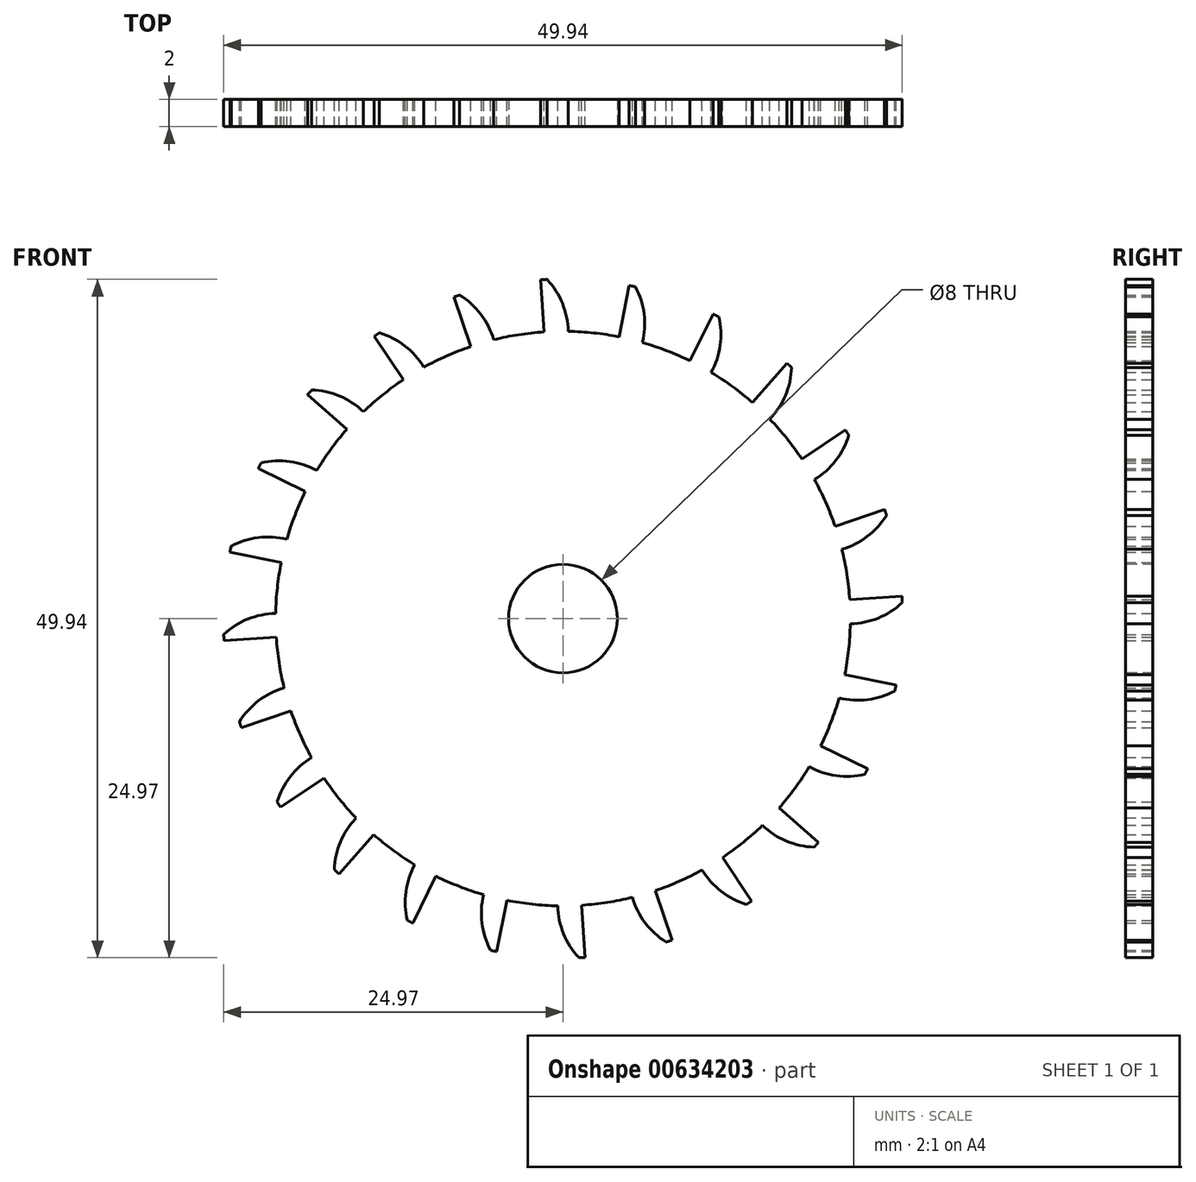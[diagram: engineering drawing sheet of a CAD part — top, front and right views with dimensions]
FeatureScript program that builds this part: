
annotation { "Feature Type Name" : "Feature", "Feature Type Description" : "" }
export const myFeature = defineFeature(function(context is Context, id is Id, definition is map)
    precondition{}
    {
        {
            var Q0;
            Q0=qCreatedBy(makeId("Front.planeOp"),FACE);
            var sketch = newSketch(context, id + "F0", { "sketchPlane" : qUnion([Q0])});
            skCircle(sketch, "E0", {"center": v(0, 0) * mm, "radius": 25 * mm, "construction": true});
            skCircle(sketch, "E1", {"center": v(0, 0) * mm, "radius": 23.1 * mm, "construction": true});
            skCircle(sketch, "E2", {"center": v(0, 0) * mm, "radius": 21.15 * mm});
            skLineSegment(sketch, "E3", {"start": v(0, 0) * mm, "end": v(0, 32.17) * mm, "construction": true});
            skLineSegment(sketch, "E4", {"start": v(0, 0) * mm, "end": v(-2.05, 31.22) * mm});
            skLineSegment(sketch, "E5", {"start": v(0, 23.1) * mm, "end": v(-31.77, 23.1) * mm, "construction": true});
            skLineSegment(sketch, "E6", {"start": v(0, 23.1) * mm, "end": v(-30.03, 12.17) * mm, "construction": true});
            skCircle(sketch, "E7", {"center": v(0, 0) * mm, "radius": 21.7 * mm, "construction": true});
            skCircle(sketch, "E8", {"center": v(0, 23.1) * mm, "radius": 5.75 * mm, "construction": true});
            skCircle(sketch, "E9", {"center": v(-5.37, 21.03) * mm, "radius": 5.75 * mm, "construction": true});
            skArc(sketch, "E10", {"start": v(0.38, 21.15) * mm, "mid": v(-0.04, 23.2) * mm, "end": v(-1.18, 24.97) * mm});
            skArc(sketch, "E11.MirrorCS", {"start": v(-3.14, 20.92) * mm, "mid": v(-2.99, 23.01) * mm, "end": v(-2.1, 24.91) * mm});
            skArc(sketch, "E12", {"start": v(-1.18, 24.97) * mm, "mid": v(-1.64, 24.95) * mm, "end": v(-2.1, 24.91) * mm});
            skSolve(sketch);
        }
        {
            var Q0;
            {var subQ0=sQuery(id+"F0.wireOp",EDGE,"E2");var subQ1=makeQuery(id+"F0.imprint","INTERSECT",VERTEX,{"derivedFrom":[subQ0,sQuery(id+"F0.wireOp",EDGE,"E10")]});Q0=makeQuery(id+"F0.imprint","IMPRINT",FACE,{"disambiguationData":[TD([[makeQuery(id+"F0.imprint","IMPRINT",EDGE,{"disambiguationData":[TD([[subQ1,-1.0]])],"derivedFrom":subQ0}),1.0]])]});}
            var Q1;
            {var subQ0=sQuery(id+"F0.wireOp",EDGE,"E11.MirrorCS");Q1=makeQuery(id+"F0.imprint","IMPRINT",FACE,{"disambiguationData":[TD([[makeQuery(id+"F0.imprint","IMPRINT",EDGE,{"derivedFrom":subQ0}),-1.0]])]});}
            var Q2;
            {var subQ0=sQuery(id+"F0.wireOp",EDGE,"E10");Q2=makeQuery(id+"F0.imprint","IMPRINT",FACE,{"disambiguationData":[TD([[makeQuery(id+"F0.imprint","IMPRINT",EDGE,{"derivedFrom":subQ0}),1.0]])]});}
            extrude(context, id + "F1", {"entities" : qUnion([Q0, Q1, Q2]), "depth" : 2 * mm, "offsetDistance" : 25 * mm});
        }
        {
            var Q0;
            Q0=makeQuery(id+"F1.opExtrude","SWEPT_BODY",BODY,{"disambiguationData":[OSD([sQuery(id+"F0.wireOp",EDGE,"E2"),sQuery(id+"F0.wireOp",EDGE,"E10"),sQuery(id+"F0.wireOp",EDGE,"E11.MirrorCS"),sQuery(id+"F0.wireOp",EDGE,"E12")])]});
            var Q1;
            Q1=makeQuery(id+"F1.opExtrude","CAP_EDGE",EDGE,{"disambiguationData":[OSD([sQuery(id+"F0.wireOp",EDGE,"E2")])],"isStart":true});
            circularPattern(context, id + "F2", {"operationType" : NewBodyOperationType.ADD, "entities" : qUnion([Q0]), "axis" : qUnion([Q1]), "angle" : 360 * degree, "instanceCount" : 24, "equalSpace" : true});
        }
        {
            var Q0;
            {var subQ0=makeQuery(id+"F1.opExtrude","CAP_FACE",FACE,{"disambiguationData":[OSD([sQuery(id+"F0.wireOp",EDGE,"E2"),sQuery(id+"F0.wireOp",EDGE,"E10"),sQuery(id+"F0.wireOp",EDGE,"E11.MirrorCS"),sQuery(id+"F0.wireOp",EDGE,"E12")])],"isStart":false});Q0=makeQuery(id+"F2.boolean.opBoolean","MERGE",FACE,{"derivedFrom":[subQ0,makeQuery(id+"F2.opPattern","COPY",FACE,{"derivedFrom":subQ0,"instanceName":"1"}),makeQuery(id+"F2.opPattern","COPY",FACE,{"derivedFrom":subQ0,"instanceName":"2"}),makeQuery(id+"F2.opPattern","COPY",FACE,{"derivedFrom":subQ0,"instanceName":"3"}),makeQuery(id+"F2.opPattern","COPY",FACE,{"derivedFrom":subQ0,"instanceName":"4"}),makeQuery(id+"F2.opPattern","COPY",FACE,{"derivedFrom":subQ0,"instanceName":"5"}),makeQuery(id+"F2.opPattern","COPY",FACE,{"derivedFrom":subQ0,"instanceName":"6"}),makeQuery(id+"F2.opPattern","COPY",FACE,{"derivedFrom":subQ0,"instanceName":"7"}),makeQuery(id+"F2.opPattern","COPY",FACE,{"derivedFrom":subQ0,"instanceName":"8"}),makeQuery(id+"F2.opPattern","COPY",FACE,{"derivedFrom":subQ0,"instanceName":"9"}),makeQuery(id+"F2.opPattern","COPY",FACE,{"derivedFrom":subQ0,"instanceName":"10"}),makeQuery(id+"F2.opPattern","COPY",FACE,{"derivedFrom":subQ0,"instanceName":"11"}),makeQuery(id+"F2.opPattern","COPY",FACE,{"derivedFrom":subQ0,"instanceName":"12"}),makeQuery(id+"F2.opPattern","COPY",FACE,{"derivedFrom":subQ0,"instanceName":"13"}),makeQuery(id+"F2.opPattern","COPY",FACE,{"derivedFrom":subQ0,"instanceName":"14"}),makeQuery(id+"F2.opPattern","COPY",FACE,{"derivedFrom":subQ0,"instanceName":"15"}),makeQuery(id+"F2.opPattern","COPY",FACE,{"derivedFrom":subQ0,"instanceName":"16"}),makeQuery(id+"F2.opPattern","COPY",FACE,{"derivedFrom":subQ0,"instanceName":"17"}),makeQuery(id+"F2.opPattern","COPY",FACE,{"derivedFrom":subQ0,"instanceName":"18"}),makeQuery(id+"F2.opPattern","COPY",FACE,{"derivedFrom":subQ0,"instanceName":"19"}),makeQuery(id+"F2.opPattern","COPY",FACE,{"derivedFrom":subQ0,"instanceName":"20"}),makeQuery(id+"F2.opPattern","COPY",FACE,{"derivedFrom":subQ0,"instanceName":"21"}),makeQuery(id+"F2.opPattern","COPY",FACE,{"derivedFrom":subQ0,"instanceName":"22"}),makeQuery(id+"F2.opPattern","COPY",FACE,{"derivedFrom":subQ0,"instanceName":"23"})]});}
            var sketch = newSketch(context, id + "F3", { "sketchPlane" : qUnion([Q0])});
            skPoint(sketch, "E13", {"position": v(0, 0) * mm});
            skSolve(sketch);
        }
        {
            var Q0;
            Q0=sQuery(id+"F3.wireOp",VERTEX,"E13");
            var Q1;
            Q1=makeQuery(id+"F1.opExtrude","SWEPT_BODY",BODY,{"disambiguationData":[OSD([sQuery(id+"F0.wireOp",EDGE,"E2"),sQuery(id+"F0.wireOp",EDGE,"E10"),sQuery(id+"F0.wireOp",EDGE,"E11.MirrorCS"),sQuery(id+"F0.wireOp",EDGE,"E12")])]});
            hole(context, id + "F4", {"style" : HoleStyle.SIMPLE, "endStyle" : HoleEndStyle.THROUGH, "holeDiameter" : 8 * mm, "majorDiameter" : 5 * mm, "isTappedThrough" : true, "tappedDepth" : 12 * mm, "tapClearance" : 3, "locations" : qUnion([Q0]), "scope" : qUnion([Q1])});
        }
    });
